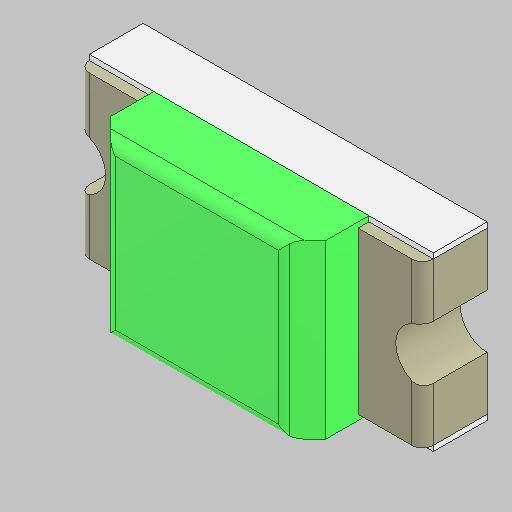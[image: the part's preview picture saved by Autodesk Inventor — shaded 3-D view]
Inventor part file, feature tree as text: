
AUTODESK INVENTOR PART (.ipt)
format: ipt  version: 2023.5 (Build 275446000, 446)  size: 158,720 bytes
history: native  units: in
note: dims shown in document units (in); Inventor stores cm internally (conversion verified against a paired STEP export)
features: fillet x2, other x2
ambient origin geometry x8: Origin, YZ Plane, XZ Plane, XY Plane, X Axis, Y Axis, Z Axis, Center Point
bodies: Solid1 (feature_tree), Solid2 (feature_tree), Solid3 (feature_tree), Solid4 (feature_tree)
feature tree (4):
  fillet  "Fillet001_(Solid)001:1"  [1 undecoded]
  fillet  "Fillet001_(Solid):1"  [1 undecoded]
  other  "Lens:1"
  other  "Base:1"
note: 2 required parameter values undecoded (feature->parameter linkage not recoverable at this tier; creation-order binding heuristic only, values carry confidence <= 0.55)
